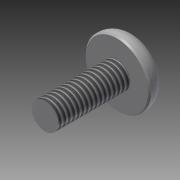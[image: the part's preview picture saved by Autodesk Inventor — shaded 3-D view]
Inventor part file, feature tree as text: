
AUTODESK INVENTOR PART (.ipt)
format: ipt  version: 2013 (Build 170138000, 138)  size: 134,656 bytes
history: native  units: in
note: dims shown in document units (in); Inventor stores cm internally (conversion verified against a paired STEP export)
features: extrude x3, sketch x2, fillet x1, thread x1, chamfer x1
ambient origin geometry x8: Origin, YZ Plane, XZ Plane, XY Plane, X Axis, Y Axis, Z Axis, Center Point
bodies: Solid1 (feature_tree)
feature tree (8):
  sketch  "Sketch1"  dims[d0=0.4538in d2=0.185in]
  extrude  "Extrusion1"  Depth=0.185in
  extrude  "Extrusion2"  Depth=0.1969in
  fillet  "Fillet1"  Radius=0.125in
  extrude  "Extrusion3"  Depth=0.1in
  thread  "Thread1"  [1 undecoded]
  chamfer  "Chamfer1"  Distance=0.075in
  sketch  "Sketch2"  dims[d3=0.5in d4=0.0in d5=0.1969in d6=0.125in d7=0.0in d8=0.1in d9=0.1969in d10=0.075in d11=0.0in d12=1.0in d13=0.0in d14=0.01in d15=0.125in d16=45.0deg]
note: 1 required parameter value undecoded (feature->parameter linkage not recoverable at this tier; creation-order binding heuristic only, values carry confidence <= 0.55)
